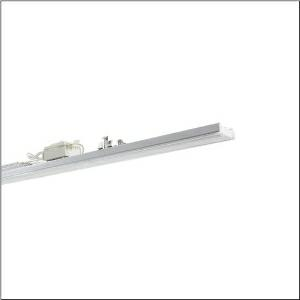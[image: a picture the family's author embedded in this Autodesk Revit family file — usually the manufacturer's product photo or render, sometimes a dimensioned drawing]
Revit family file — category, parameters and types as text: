
# Revit family: licross_r__21_recessed_ho_52tl1edv4l2s_3d33
name_source: partatom
category: Lighting Fixtures
units: mm (PartAtom-declared; Revit-internal decimal feet)

## family parameters
Cut with Voids When Loaded = No
Host = Face
Light Source = No
Part Type = Normal
Room Calculation Point = No
Round Connector Dimension = Use Diameter
Shared = No

## types (1)
- --- (1 x LED, 22130 lm, 125.6 W, 4000K)
    Apparent Load = 126 VA
    CIE Flux Codes = 85 95 99 100 100
    Color Rendering = 80
    Color Temperature = 4000K
    Default Elevation = 1800 mm
    Description = Licross® 21 Recessed HO, luminaire insert, of sheet steel, galvanised, coil coated, white, length: 2.250mm, width: 66mm, height: 67mm, LED rated luminous flux: 22.130lm, light colour: 840, control gear: DALI 2, with plug, 5-pole, with phase selection, mains connection: 220..240V, AC, 50/60Hz, rated input power: 126W, halogen-free wiring, primary light control with lens, of plastic, primary optical cover: cover, of PMMA, light emission: direct distribution, primary light characteristic: symmetric, protection rating (complete): IP40, insulation class (complete): insulation class I (protective earthing), certification: CE, ENEC, VDE, UKCA, protection symbol: D if used in an environment without relevant dust loads with corresponding accessories, impact resistance: IK06, permissible ambient temperature for indoor applications: -40..+30°C, corresponds to IFS (International Featured Standards) requirements for safety and quality in the food industry, reducing of maximum allowable ambient temperature of 5°C with ceiling mounting, LABS conformity tested according to VDMA 24364:2018-05, packaging unit: 1 piece
    Height = 58 mm
    Lamp = 1 x LED
    Lamp Light Flux = 22130 lm
    Lamp Power = 125.6 W
    Lamp count = 1
    Length = 2250 mm
    Luminous efficacy = 176 lm/W
    Manufacturer = Siteco
    ModVariant = No
    Model = 52TL1EDV4L2S
    Mounting Place = Ceiling
    Mounting Type = Pendant
    Number of Poles = 1
    OnlyDefault = Yes
    Power Factor = 1
    Product Name = Licross® 21 Recessed HO
    Product group = luminaire insert
    ProductGroupID = 902
    Protection Class = Protection class I
    Protection Degree = IP 40
    RLX_Detail_Level = 1
    RLX_Emergency_Light_Flux = 0 lm
    RLX_Emergency_Type = 0
    RLX_Emergency_Type_DB = No
    RlxData = <blob elided: 29749 chars, md5=97abdc7d>
    Socket = socket
    Standby Power = 0 W
    System Light Flux = 22129 lm
    System Power = 126 W
    Type Comments = factory setting: luminous flux: 100 % | dim-lin: 254 | 489 mA
    Type Image = l_1296930.jpg
    URL = http://relux.com
    VarID = @adj_125548
    Voltage = 0 V
    Weight = 0.00 kg
    Width = 66 mm

## geometry (parser evidence)
native form markers: Blend x4, Sweep x11
no freeform markers — native parametric forms only
